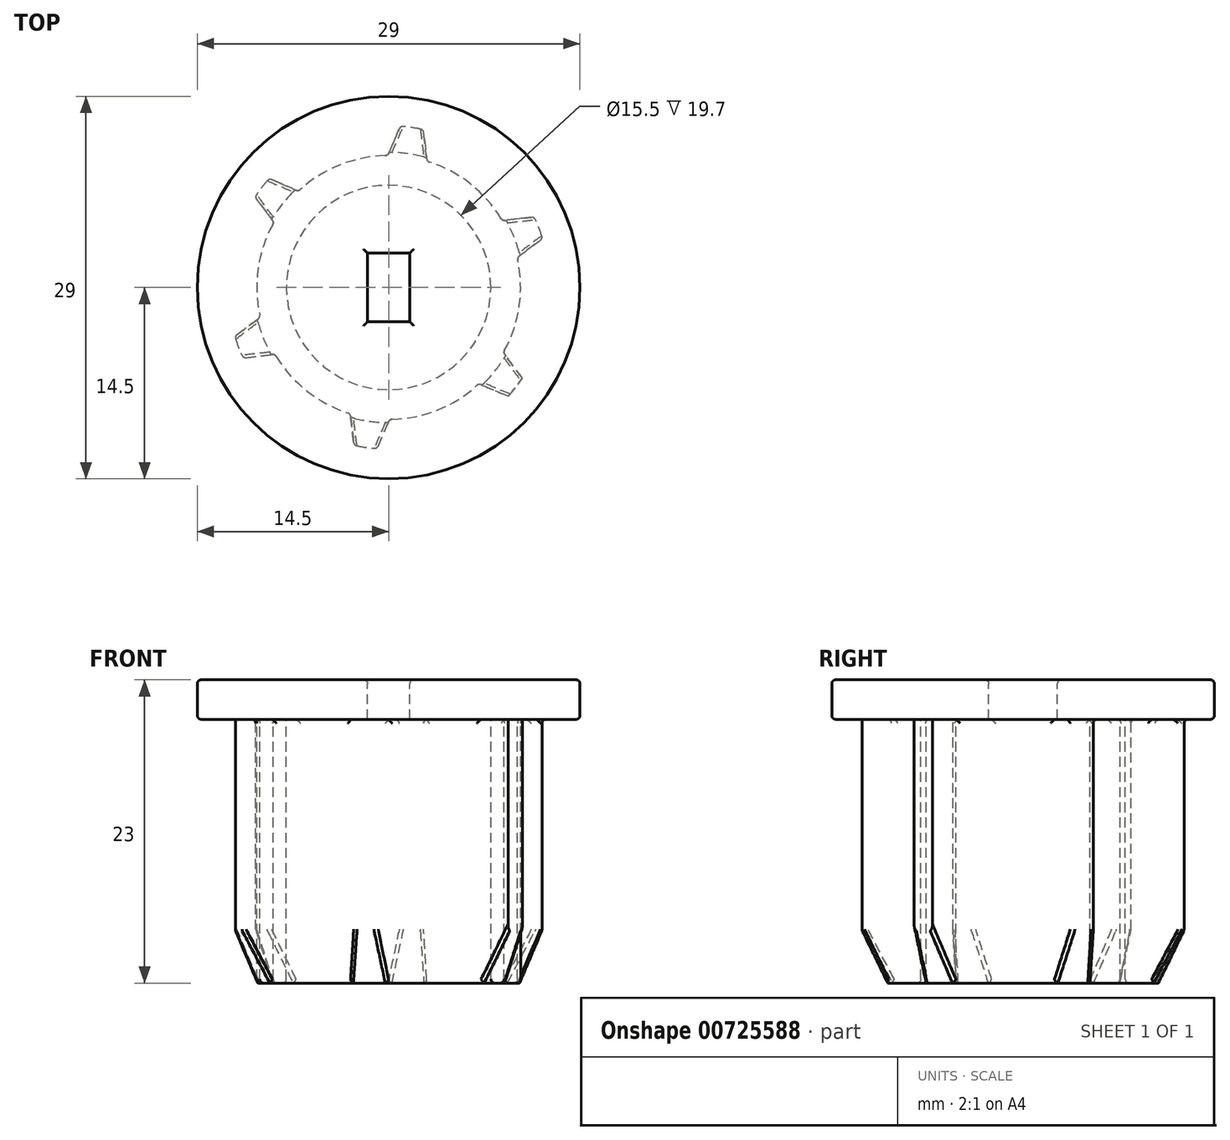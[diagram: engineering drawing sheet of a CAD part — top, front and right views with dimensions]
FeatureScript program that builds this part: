
annotation { "Feature Type Name" : "Feature", "Feature Type Description" : "" }
export const myFeature = defineFeature(function(context is Context, id is Id, definition is map)
    precondition{}
    {
        {
            var Q0;
            Q0=qCreatedBy(makeId("Top.planeOp"),FACE);
            var sketch = newSketch(context, id + "F0", { "sketchPlane" : qUnion([Q0])});
            skCircle(sketch, "E0", {"center": v(-16.6, 0) * mm, "radius": 14.5 * mm});
            skCircle(sketch, "E1", {"center": v(-16.6, 0) * mm, "radius": 12.25 * mm});
            skCircle(sketch, "E2", {"center": v(-16.6, 0) * mm, "radius": 4 * mm, "construction": true});
            skLineSegment(sketch, "E3.bottom", {"start": v(-18.2, -2.6) * mm, "end": v(-15, -2.6) * mm});
            skLineSegment(sketch, "E3.top", {"start": v(-18.2, 2.6) * mm, "end": v(-15, 2.6) * mm});
            skLineSegment(sketch, "E3.left", {"start": v(-18.2, -2.6) * mm, "end": v(-18.2, 2.6) * mm});
            skLineSegment(sketch, "E3.right", {"start": v(-15, -2.6) * mm, "end": v(-15, 2.6) * mm});
            skCircle(sketch, "E4.cCircle", {"center": v(-16.6, 0) * mm, "radius": 15 * mm, "construction": true});
            skLineSegment(sketch, "E4.0", {"start": v(-6.99, 12.2) * mm, "end": v(-2.18, 5.76) * mm});
            skLineSegment(sketch, "E4.1", {"start": v(-2.18, 5.76) * mm, "end": v(-1.23, -2.23) * mm});
            skLineSegment(sketch, "E4.2", {"start": v(-1.23, -2.23) * mm, "end": v(-4.4, -9.61) * mm});
            skLineSegment(sketch, "E4.3", {"start": v(-4.4, -9.61) * mm, "end": v(-10.84, -14.42) * mm});
            skLineSegment(sketch, "E4.4", {"start": v(-10.84, -14.42) * mm, "end": v(-18.83, -15.37) * mm});
            skLineSegment(sketch, "E4.5", {"start": v(-18.83, -15.37) * mm, "end": v(-26.21, -12.2) * mm});
            skLineSegment(sketch, "E4.6", {"start": v(-26.21, -12.2) * mm, "end": v(-31.02, -5.76) * mm});
            skLineSegment(sketch, "E4.7", {"start": v(-31.02, -5.76) * mm, "end": v(-31.97, 2.23) * mm});
            skLineSegment(sketch, "E4.8", {"start": v(-31.97, 2.23) * mm, "end": v(-28.8, 9.61) * mm});
            skLineSegment(sketch, "E4.9", {"start": v(-28.8, 9.61) * mm, "end": v(-22.36, 14.42) * mm});
            skLineSegment(sketch, "E4.10", {"start": v(-22.36, 14.42) * mm, "end": v(-14.37, 15.37) * mm});
            skLineSegment(sketch, "E4.11", {"start": v(-14.37, 15.37) * mm, "end": v(-6.99, 12.2) * mm});
            skPoint(sketch, "E4.0.midPoint", {"position": v(-4.58, 8.98) * mm});
            skLineSegment(sketch, "E5", {"start": v(-18.83, -15.37) * mm, "end": v(-20.57, -0.47) * mm});
            skLineSegment(sketch, "E6", {"start": v(-18.83, -15.37) * mm, "end": v(-12.92, -1.57) * mm});
            skLineSegment(sketch, "E7", {"start": v(-4.4, -9.61) * mm, "end": v(-18.18, -3.67) * mm});
            skLineSegment(sketch, "E8", {"start": v(-4.4, -9.61) * mm, "end": v(-13.4, 2.4) * mm});
            skLineSegment(sketch, "E9", {"start": v(-2.18, 5.76) * mm, "end": v(-14.21, -3.2) * mm});
            skLineSegment(sketch, "E10", {"start": v(-2.18, 5.76) * mm, "end": v(-17.08, 3.97) * mm});
            skLineSegment(sketch, "E11", {"start": v(-14.37, 15.37) * mm, "end": v(-12.63, 0.47) * mm});
            skLineSegment(sketch, "E12", {"start": v(-14.37, 15.37) * mm, "end": v(-20.28, 1.57) * mm});
            skLineSegment(sketch, "E13", {"start": v(-28.8, 9.61) * mm, "end": v(-15.02, 3.67) * mm});
            skLineSegment(sketch, "E14", {"start": v(-28.8, 9.61) * mm, "end": v(-19.8, -2.4) * mm});
            skLineSegment(sketch, "E15", {"start": v(-31.02, -5.76) * mm, "end": v(-18.99, 3.2) * mm});
            skLineSegment(sketch, "E16", {"start": v(-31.02, -5.76) * mm, "end": v(-16.12, -3.97) * mm});
            skCircle(sketch, "E17", {"center": v(-16.6, 0) * mm, "radius": 10 * mm});
            skCircle(sketch, "E18", {"center": v(-16.6, 0) * mm, "radius": 7.75 * mm});
            skSolve(sketch);
        }
        {
            var Q0;
            Q0=qCreatedBy(makeId("Front.planeOp"),FACE);
            var sketch = newSketch(context, id + "F1", { "sketchPlane" : qUnion([Q0])});
            skLineSegment(sketch, "E19", {"start": v(-32.68, -23) * mm, "end": v(-0.52, -23) * mm});
            skLineSegment(sketch, "E20", {"start": v(-32.68, -20) * mm, "end": v(-0.52, -20) * mm});
            skLineSegment(sketch, "E21", {"start": v(-32.68, -3) * mm, "end": v(-0.52, -3) * mm});
            skLineSegment(sketch, "E22", {"start": v(-32.68, 0) * mm, "end": v(-0.52, 0) * mm});
            skSolve(sketch);
        }
        {
            var Q0;
            {var subQ0=sQuery(id+"F0.wireOp",EDGE,"E17");var subQ1=sQuery(id+"F0.wireOp",EDGE,"E10");var subQ2=makeQuery(id+"F0.imprint","INTERSECT",VERTEX,{"derivedFrom":[subQ1,subQ0]});Q0=makeQuery(id+"F0.imprint","IMPRINT",FACE,{"disambiguationData":[TD([[makeQuery(id+"F0.imprint","IMPRINT",EDGE,{"disambiguationData":[TD([[subQ2,-1.0]])],"derivedFrom":subQ1}),-1.0]])]});}
            var Q1;
            {var subQ0=sQuery(id+"F0.wireOp",EDGE,"E10");var subQ1=sQuery(id+"F0.wireOp",EDGE,"E1");var subQ2=makeQuery(id+"F0.imprint","INTERSECT",VERTEX,{"derivedFrom":[subQ1,subQ0]});Q1=makeQuery(id+"F0.imprint","IMPRINT",FACE,{"disambiguationData":[TD([[makeQuery(id+"F0.imprint","IMPRINT",EDGE,{"disambiguationData":[TD([[subQ2,1.0]])],"derivedFrom":subQ1}),1.0]])]});}
            var Q2;
            {var subQ0=sQuery(id+"F0.wireOp",EDGE,"E17");var subQ1=sQuery(id+"F0.wireOp",EDGE,"E9");var subQ2=makeQuery(id+"F0.imprint","INTERSECT",VERTEX,{"derivedFrom":[subQ1,subQ0]});Q2=makeQuery(id+"F0.imprint","IMPRINT",FACE,{"disambiguationData":[TD([[makeQuery(id+"F0.imprint","IMPRINT",EDGE,{"disambiguationData":[TD([[subQ2,-1.0]])],"derivedFrom":subQ1}),-1.0]])]});}
            var Q3;
            {var subQ0=sQuery(id+"F0.wireOp",EDGE,"E17");var subQ1=sQuery(id+"F0.wireOp",EDGE,"E8");var subQ2=makeQuery(id+"F0.imprint","INTERSECT",VERTEX,{"derivedFrom":[subQ1,subQ0]});Q3=makeQuery(id+"F0.imprint","IMPRINT",FACE,{"disambiguationData":[TD([[makeQuery(id+"F0.imprint","IMPRINT",EDGE,{"disambiguationData":[TD([[subQ2,-1.0]])],"derivedFrom":subQ1}),-1.0]])]});}
            var Q4;
            {var subQ0=sQuery(id+"F0.wireOp",EDGE,"E7");var subQ1=sQuery(id+"F0.wireOp",EDGE,"E1");var subQ2=makeQuery(id+"F0.imprint","INTERSECT",VERTEX,{"derivedFrom":[subQ1,subQ0]});Q4=makeQuery(id+"F0.imprint","IMPRINT",FACE,{"disambiguationData":[TD([[makeQuery(id+"F0.imprint","IMPRINT",EDGE,{"disambiguationData":[TD([[subQ2,-1.0]])],"derivedFrom":subQ1}),1.0]])]});}
            var Q5;
            {var subQ0=sQuery(id+"F0.wireOp",EDGE,"E17");var subQ1=sQuery(id+"F0.wireOp",EDGE,"E7");var subQ2=makeQuery(id+"F0.imprint","INTERSECT",VERTEX,{"derivedFrom":[subQ1,subQ0]});Q5=makeQuery(id+"F0.imprint","IMPRINT",FACE,{"disambiguationData":[TD([[makeQuery(id+"F0.imprint","IMPRINT",EDGE,{"disambiguationData":[TD([[subQ2,-1.0]])],"derivedFrom":subQ1}),-1.0]])]});}
            var Q6;
            {var subQ0=sQuery(id+"F0.wireOp",EDGE,"E17");var subQ1=sQuery(id+"F0.wireOp",EDGE,"E6");var subQ2=makeQuery(id+"F0.imprint","INTERSECT",VERTEX,{"derivedFrom":[subQ1,subQ0]});Q6=makeQuery(id+"F0.imprint","IMPRINT",FACE,{"disambiguationData":[TD([[makeQuery(id+"F0.imprint","IMPRINT",EDGE,{"disambiguationData":[TD([[subQ2,-1.0]])],"derivedFrom":subQ1}),-1.0]])]});}
            var Q7;
            {var subQ0=sQuery(id+"F0.wireOp",EDGE,"E17");var subQ1=sQuery(id+"F0.wireOp",EDGE,"E5");var subQ2=makeQuery(id+"F0.imprint","INTERSECT",VERTEX,{"derivedFrom":[subQ1,subQ0]});Q7=makeQuery(id+"F0.imprint","IMPRINT",FACE,{"disambiguationData":[TD([[makeQuery(id+"F0.imprint","IMPRINT",EDGE,{"disambiguationData":[TD([[subQ2,-1.0]])],"derivedFrom":subQ1}),-1.0]])]});}
            var Q8;
            {var subQ0=sQuery(id+"F0.wireOp",EDGE,"E5");var subQ1=sQuery(id+"F0.wireOp",EDGE,"E1");var subQ2=makeQuery(id+"F0.imprint","INTERSECT",VERTEX,{"derivedFrom":[subQ1,subQ0]});Q8=makeQuery(id+"F0.imprint","IMPRINT",FACE,{"disambiguationData":[TD([[makeQuery(id+"F0.imprint","IMPRINT",EDGE,{"disambiguationData":[TD([[subQ2,-1.0]])],"derivedFrom":subQ1}),1.0]])]});}
            var Q9;
            {var subQ0=sQuery(id+"F0.wireOp",EDGE,"E17");var subQ1=sQuery(id+"F0.wireOp",EDGE,"E5");var subQ2=makeQuery(id+"F0.imprint","INTERSECT",VERTEX,{"derivedFrom":[subQ1,subQ0]});Q9=makeQuery(id+"F0.imprint","IMPRINT",FACE,{"disambiguationData":[TD([[makeQuery(id+"F0.imprint","IMPRINT",EDGE,{"disambiguationData":[TD([[subQ2,-1.0]])],"derivedFrom":subQ1}),1.0]])]});}
            var Q10;
            {var subQ0=sQuery(id+"F0.wireOp",EDGE,"E17");var subQ1=sQuery(id+"F0.wireOp",EDGE,"E15");var subQ2=makeQuery(id+"F0.imprint","INTERSECT",VERTEX,{"derivedFrom":[subQ1,subQ0]});Q10=makeQuery(id+"F0.imprint","IMPRINT",FACE,{"disambiguationData":[TD([[makeQuery(id+"F0.imprint","IMPRINT",EDGE,{"disambiguationData":[TD([[subQ2,-1.0]])],"derivedFrom":subQ1}),-1.0]])]});}
            var Q11;
            {var subQ0=sQuery(id+"F0.wireOp",EDGE,"E15");var subQ1=sQuery(id+"F0.wireOp",EDGE,"E1");var subQ2=makeQuery(id+"F0.imprint","INTERSECT",VERTEX,{"derivedFrom":[subQ1,subQ0]});Q11=makeQuery(id+"F0.imprint","IMPRINT",FACE,{"disambiguationData":[TD([[makeQuery(id+"F0.imprint","IMPRINT",EDGE,{"disambiguationData":[TD([[subQ2,-1.0]])],"derivedFrom":subQ1}),1.0]])]});}
            var Q12;
            {var subQ0=sQuery(id+"F0.wireOp",EDGE,"E17");var subQ1=sQuery(id+"F0.wireOp",EDGE,"E14");var subQ2=makeQuery(id+"F0.imprint","INTERSECT",VERTEX,{"derivedFrom":[subQ1,subQ0]});Q12=makeQuery(id+"F0.imprint","IMPRINT",FACE,{"disambiguationData":[TD([[makeQuery(id+"F0.imprint","IMPRINT",EDGE,{"disambiguationData":[TD([[subQ2,-1.0]])],"derivedFrom":subQ1}),-1.0]])]});}
            var Q13;
            {var subQ0=sQuery(id+"F0.wireOp",EDGE,"E17");var subQ1=sQuery(id+"F0.wireOp",EDGE,"E13");var subQ2=makeQuery(id+"F0.imprint","INTERSECT",VERTEX,{"derivedFrom":[subQ1,subQ0]});Q13=makeQuery(id+"F0.imprint","IMPRINT",FACE,{"disambiguationData":[TD([[makeQuery(id+"F0.imprint","IMPRINT",EDGE,{"disambiguationData":[TD([[subQ2,-1.0]])],"derivedFrom":subQ1}),-1.0]])]});}
            var Q14;
            {var subQ0=sQuery(id+"F0.wireOp",EDGE,"E13");var subQ1=sQuery(id+"F0.wireOp",EDGE,"E1");var subQ2=makeQuery(id+"F0.imprint","INTERSECT",VERTEX,{"derivedFrom":[subQ1,subQ0]});Q14=makeQuery(id+"F0.imprint","IMPRINT",FACE,{"disambiguationData":[TD([[makeQuery(id+"F0.imprint","IMPRINT",EDGE,{"disambiguationData":[TD([[subQ2,-1.0]])],"derivedFrom":subQ1}),1.0]])]});}
            var Q15;
            {var subQ0=sQuery(id+"F0.wireOp",EDGE,"E17");var subQ1=sQuery(id+"F0.wireOp",EDGE,"E12");var subQ2=makeQuery(id+"F0.imprint","INTERSECT",VERTEX,{"derivedFrom":[subQ1,subQ0]});Q15=makeQuery(id+"F0.imprint","IMPRINT",FACE,{"disambiguationData":[TD([[makeQuery(id+"F0.imprint","IMPRINT",EDGE,{"disambiguationData":[TD([[subQ2,-1.0]])],"derivedFrom":subQ1}),-1.0]])]});}
            var Q16;
            {var subQ0=sQuery(id+"F0.wireOp",EDGE,"E17");var subQ1=sQuery(id+"F0.wireOp",EDGE,"E11");var subQ2=makeQuery(id+"F0.imprint","INTERSECT",VERTEX,{"derivedFrom":[subQ1,subQ0]});Q16=makeQuery(id+"F0.imprint","IMPRINT",FACE,{"disambiguationData":[TD([[makeQuery(id+"F0.imprint","IMPRINT",EDGE,{"disambiguationData":[TD([[subQ2,-1.0]])],"derivedFrom":subQ1}),-1.0]])]});}
            var Q17;
            {var subQ0=sQuery(id+"F0.wireOp",EDGE,"E11");var subQ1=sQuery(id+"F0.wireOp",EDGE,"E1");var subQ2=makeQuery(id+"F0.imprint","INTERSECT",VERTEX,{"derivedFrom":[subQ1,subQ0]});Q17=makeQuery(id+"F0.imprint","IMPRINT",FACE,{"disambiguationData":[TD([[makeQuery(id+"F0.imprint","IMPRINT",EDGE,{"disambiguationData":[TD([[subQ2,-1.0]])],"derivedFrom":subQ1}),1.0]])]});}
            var Q18;
            Q18=sQuery(id+"F1.wireOp",VERTEX,"E19.start");
            extrude(context, id + "F2", {"entities" : qUnion([Q0, Q1, Q2, Q3, Q4, Q5, Q6, Q7, Q8, Q9, Q10, Q11, Q12, Q13, Q14, Q15, Q16, Q17]), "endBound" : BoundingType.UP_TO_VERTEX, "oppositeDirection" : true, "depth" : 25 * mm, "endBoundEntityVertex" : qUnion([Q18]), "offsetDistance" : 25 * mm});
        }
        {
            var Q0;
            {var subQ0=sQuery(id+"F0.wireOp",EDGE,"E12");var subQ1=sQuery(id+"F0.wireOp",EDGE,"E1");var subQ2=makeQuery(id+"F0.imprint","INTERSECT",VERTEX,{"derivedFrom":[subQ1,subQ0]});Q0=makeQuery(id+"F0.imprint","IMPRINT",FACE,{"disambiguationData":[TD([[makeQuery(id+"F0.imprint","IMPRINT",EDGE,{"disambiguationData":[TD([[subQ2,-1.0]])],"derivedFrom":subQ1}),1.0]])]});}
            var Q1;
            {var subQ0=sQuery(id+"F0.wireOp",EDGE,"E12");var subQ1=sQuery(id+"F0.wireOp",EDGE,"E0");var subQ2=makeQuery(id+"F0.imprint","INTERSECT",VERTEX,{"derivedFrom":[subQ1,subQ0]});Q1=makeQuery(id+"F0.imprint","IMPRINT",FACE,{"disambiguationData":[TD([[makeQuery(id+"F0.imprint","IMPRINT",EDGE,{"disambiguationData":[TD([[subQ2,-1.0]])],"derivedFrom":subQ1}),1.0]])]});}
            var Q2;
            {var subQ0=sQuery(id+"F0.wireOp",EDGE,"E11");var subQ1=sQuery(id+"F0.wireOp",EDGE,"E0");var subQ2=makeQuery(id+"F0.imprint","INTERSECT",VERTEX,{"derivedFrom":[subQ1,subQ0]});Q2=makeQuery(id+"F0.imprint","IMPRINT",FACE,{"disambiguationData":[TD([[makeQuery(id+"F0.imprint","IMPRINT",EDGE,{"disambiguationData":[TD([[subQ2,-1.0]])],"derivedFrom":subQ1}),1.0]])]});}
            var Q3;
            {var subQ0=sQuery(id+"F0.wireOp",EDGE,"E10");var subQ1=sQuery(id+"F0.wireOp",EDGE,"E0");var subQ2=makeQuery(id+"F0.imprint","INTERSECT",VERTEX,{"derivedFrom":[subQ1,subQ0]});Q3=makeQuery(id+"F0.imprint","IMPRINT",FACE,{"disambiguationData":[TD([[makeQuery(id+"F0.imprint","IMPRINT",EDGE,{"disambiguationData":[TD([[subQ2,-1.0]])],"derivedFrom":subQ1}),1.0]])]});}
            var Q4;
            {var subQ0=sQuery(id+"F0.wireOp",EDGE,"E10");var subQ1=sQuery(id+"F0.wireOp",EDGE,"E1");var subQ2=makeQuery(id+"F0.imprint","INTERSECT",VERTEX,{"derivedFrom":[subQ1,subQ0]});Q4=makeQuery(id+"F0.imprint","IMPRINT",FACE,{"disambiguationData":[TD([[makeQuery(id+"F0.imprint","IMPRINT",EDGE,{"disambiguationData":[TD([[subQ2,-1.0]])],"derivedFrom":subQ1}),1.0]])]});}
            var Q5;
            {var subQ0=sQuery(id+"F0.wireOp",EDGE,"E11");var subQ1=sQuery(id+"F0.wireOp",EDGE,"E1");var subQ2=makeQuery(id+"F0.imprint","INTERSECT",VERTEX,{"derivedFrom":[subQ1,subQ0]});Q5=makeQuery(id+"F0.imprint","IMPRINT",FACE,{"disambiguationData":[TD([[makeQuery(id+"F0.imprint","IMPRINT",EDGE,{"disambiguationData":[TD([[subQ2,-1.0]])],"derivedFrom":subQ1}),1.0]])]});}
            var Q6;
            {var subQ0=sQuery(id+"F0.wireOp",EDGE,"E17");var subQ1=sQuery(id+"F0.wireOp",EDGE,"E10");var subQ2=makeQuery(id+"F0.imprint","INTERSECT",VERTEX,{"derivedFrom":[subQ1,subQ0]});Q6=makeQuery(id+"F0.imprint","IMPRINT",FACE,{"disambiguationData":[TD([[makeQuery(id+"F0.imprint","IMPRINT",EDGE,{"disambiguationData":[TD([[subQ2,-1.0]])],"derivedFrom":subQ1}),-1.0]])]});}
            var Q7;
            {var subQ0=sQuery(id+"F0.wireOp",EDGE,"E17");var subQ1=sQuery(id+"F0.wireOp",EDGE,"E9");var subQ2=makeQuery(id+"F0.imprint","INTERSECT",VERTEX,{"derivedFrom":[subQ1,subQ0]});Q7=makeQuery(id+"F0.imprint","IMPRINT",FACE,{"disambiguationData":[TD([[makeQuery(id+"F0.imprint","IMPRINT",EDGE,{"disambiguationData":[TD([[subQ2,-1.0]])],"derivedFrom":subQ1}),-1.0]])]});}
            var Q8;
            {var subQ0=sQuery(id+"F0.wireOp",EDGE,"E10");var subQ1=sQuery(id+"F0.wireOp",EDGE,"E1");var subQ2=makeQuery(id+"F0.imprint","INTERSECT",VERTEX,{"derivedFrom":[subQ1,subQ0]});Q8=makeQuery(id+"F0.imprint","IMPRINT",FACE,{"disambiguationData":[TD([[makeQuery(id+"F0.imprint","IMPRINT",EDGE,{"disambiguationData":[TD([[subQ2,1.0]])],"derivedFrom":subQ1}),1.0]])]});}
            var Q9;
            {var subQ0=sQuery(id+"F0.wireOp",EDGE,"E10");var subQ1=sQuery(id+"F0.wireOp",EDGE,"E0");var subQ2=makeQuery(id+"F0.imprint","INTERSECT",VERTEX,{"derivedFrom":[subQ1,subQ0]});Q9=makeQuery(id+"F0.imprint","IMPRINT",FACE,{"disambiguationData":[TD([[makeQuery(id+"F0.imprint","IMPRINT",EDGE,{"disambiguationData":[TD([[subQ2,1.0]])],"derivedFrom":subQ1}),1.0]])]});}
            var Q10;
            {var subQ0=sQuery(id+"F0.wireOp",EDGE,"E9");var subQ1=sQuery(id+"F0.wireOp",EDGE,"E1");var subQ2=makeQuery(id+"F0.imprint","INTERSECT",VERTEX,{"derivedFrom":[subQ1,subQ0]});Q10=makeQuery(id+"F0.imprint","IMPRINT",FACE,{"disambiguationData":[TD([[makeQuery(id+"F0.imprint","IMPRINT",EDGE,{"disambiguationData":[TD([[subQ2,1.0]])],"derivedFrom":subQ1}),1.0]])]});}
            var Q11;
            {var subQ0=sQuery(id+"F0.wireOp",EDGE,"E6");var subQ1=sQuery(id+"F0.wireOp",EDGE,"E0");var subQ2=makeQuery(id+"F0.imprint","INTERSECT",VERTEX,{"derivedFrom":[subQ1,subQ0]});Q11=makeQuery(id+"F0.imprint","IMPRINT",FACE,{"disambiguationData":[TD([[makeQuery(id+"F0.imprint","IMPRINT",EDGE,{"disambiguationData":[TD([[subQ2,-1.0]])],"derivedFrom":subQ1}),1.0]])]});}
            var Q12;
            {var subQ0=sQuery(id+"F0.wireOp",EDGE,"E5");var subQ1=sQuery(id+"F0.wireOp",EDGE,"E0");var subQ2=makeQuery(id+"F0.imprint","INTERSECT",VERTEX,{"derivedFrom":[subQ1,subQ0]});Q12=makeQuery(id+"F0.imprint","IMPRINT",FACE,{"disambiguationData":[TD([[makeQuery(id+"F0.imprint","IMPRINT",EDGE,{"disambiguationData":[TD([[subQ2,-1.0]])],"derivedFrom":subQ1}),1.0]])]});}
            var Q13;
            {var subQ0=sQuery(id+"F0.wireOp",EDGE,"E5");var subQ1=sQuery(id+"F0.wireOp",EDGE,"E1");var subQ2=makeQuery(id+"F0.imprint","INTERSECT",VERTEX,{"derivedFrom":[subQ1,subQ0]});Q13=makeQuery(id+"F0.imprint","IMPRINT",FACE,{"disambiguationData":[TD([[makeQuery(id+"F0.imprint","IMPRINT",EDGE,{"disambiguationData":[TD([[subQ2,-1.0]])],"derivedFrom":subQ1}),1.0]])]});}
            var Q14;
            {var subQ0=sQuery(id+"F0.wireOp",EDGE,"E15");var subQ1=sQuery(id+"F0.wireOp",EDGE,"E1");var subQ2=makeQuery(id+"F0.imprint","INTERSECT",VERTEX,{"derivedFrom":[subQ1,subQ0]});Q14=makeQuery(id+"F0.imprint","IMPRINT",FACE,{"disambiguationData":[TD([[makeQuery(id+"F0.imprint","IMPRINT",EDGE,{"disambiguationData":[TD([[subQ2,-1.0]])],"derivedFrom":subQ1}),1.0]])]});}
            var Q15;
            {var subQ0=sQuery(id+"F0.wireOp",EDGE,"E17");var subQ1=sQuery(id+"F0.wireOp",EDGE,"E15");var subQ2=makeQuery(id+"F0.imprint","INTERSECT",VERTEX,{"derivedFrom":[subQ1,subQ0]});Q15=makeQuery(id+"F0.imprint","IMPRINT",FACE,{"disambiguationData":[TD([[makeQuery(id+"F0.imprint","IMPRINT",EDGE,{"disambiguationData":[TD([[subQ2,-1.0]])],"derivedFrom":subQ1}),-1.0]])]});}
            var Q16;
            {var subQ0=sQuery(id+"F0.wireOp",EDGE,"E9");var subQ1=sQuery(id+"F0.wireOp",EDGE,"E0");var subQ2=makeQuery(id+"F0.imprint","INTERSECT",VERTEX,{"derivedFrom":[subQ1,subQ0]});Q16=makeQuery(id+"F0.imprint","IMPRINT",FACE,{"disambiguationData":[TD([[makeQuery(id+"F0.imprint","IMPRINT",EDGE,{"disambiguationData":[TD([[subQ2,1.0]])],"derivedFrom":subQ1}),1.0]])]});}
            var Q17;
            {var subQ0=sQuery(id+"F0.wireOp",EDGE,"E7");var subQ1=sQuery(id+"F0.wireOp",EDGE,"E0");var subQ2=makeQuery(id+"F0.imprint","INTERSECT",VERTEX,{"derivedFrom":[subQ1,subQ0]});Q17=makeQuery(id+"F0.imprint","IMPRINT",FACE,{"disambiguationData":[TD([[makeQuery(id+"F0.imprint","IMPRINT",EDGE,{"disambiguationData":[TD([[subQ2,-1.0]])],"derivedFrom":subQ1}),1.0]])]});}
            var Q18;
            {var subQ0=sQuery(id+"F0.wireOp",EDGE,"E7");var subQ1=sQuery(id+"F0.wireOp",EDGE,"E1");var subQ2=makeQuery(id+"F0.imprint","INTERSECT",VERTEX,{"derivedFrom":[subQ1,subQ0]});Q18=makeQuery(id+"F0.imprint","IMPRINT",FACE,{"disambiguationData":[TD([[makeQuery(id+"F0.imprint","IMPRINT",EDGE,{"disambiguationData":[TD([[subQ2,-1.0]])],"derivedFrom":subQ1}),1.0]])]});}
            var Q19;
            {var subQ0=sQuery(id+"F0.wireOp",EDGE,"E6");var subQ1=sQuery(id+"F0.wireOp",EDGE,"E1");var subQ2=makeQuery(id+"F0.imprint","INTERSECT",VERTEX,{"derivedFrom":[subQ1,subQ0]});Q19=makeQuery(id+"F0.imprint","IMPRINT",FACE,{"disambiguationData":[TD([[makeQuery(id+"F0.imprint","IMPRINT",EDGE,{"disambiguationData":[TD([[subQ2,-1.0]])],"derivedFrom":subQ1}),1.0]])]});}
            var Q20;
            {var subQ0=sQuery(id+"F0.wireOp",EDGE,"E16");var subQ1=sQuery(id+"F0.wireOp",EDGE,"E1");var subQ2=makeQuery(id+"F0.imprint","INTERSECT",VERTEX,{"derivedFrom":[subQ1,subQ0]});Q20=makeQuery(id+"F0.imprint","IMPRINT",FACE,{"disambiguationData":[TD([[makeQuery(id+"F0.imprint","IMPRINT",EDGE,{"disambiguationData":[TD([[subQ2,-1.0]])],"derivedFrom":subQ1}),1.0]])]});}
            var Q21;
            {var subQ0=sQuery(id+"F0.wireOp",EDGE,"E16");var subQ1=sQuery(id+"F0.wireOp",EDGE,"E0");var subQ2=makeQuery(id+"F0.imprint","INTERSECT",VERTEX,{"derivedFrom":[subQ1,subQ0]});Q21=makeQuery(id+"F0.imprint","IMPRINT",FACE,{"disambiguationData":[TD([[makeQuery(id+"F0.imprint","IMPRINT",EDGE,{"disambiguationData":[TD([[subQ2,-1.0]])],"derivedFrom":subQ1}),1.0]])]});}
            var Q22;
            {var subQ0=sQuery(id+"F0.wireOp",EDGE,"E15");var subQ1=sQuery(id+"F0.wireOp",EDGE,"E0");var subQ2=makeQuery(id+"F0.imprint","INTERSECT",VERTEX,{"derivedFrom":[subQ1,subQ0]});Q22=makeQuery(id+"F0.imprint","IMPRINT",FACE,{"disambiguationData":[TD([[makeQuery(id+"F0.imprint","IMPRINT",EDGE,{"disambiguationData":[TD([[subQ2,-1.0]])],"derivedFrom":subQ1}),1.0]])]});}
            var Q23;
            {var subQ0=sQuery(id+"F0.wireOp",EDGE,"E14");var subQ1=sQuery(id+"F0.wireOp",EDGE,"E0");var subQ2=makeQuery(id+"F0.imprint","INTERSECT",VERTEX,{"derivedFrom":[subQ1,subQ0]});Q23=makeQuery(id+"F0.imprint","IMPRINT",FACE,{"disambiguationData":[TD([[makeQuery(id+"F0.imprint","IMPRINT",EDGE,{"disambiguationData":[TD([[subQ2,-1.0]])],"derivedFrom":subQ1}),1.0]])]});}
            var Q24;
            {var subQ0=sQuery(id+"F0.wireOp",EDGE,"E14");var subQ1=sQuery(id+"F0.wireOp",EDGE,"E1");var subQ2=makeQuery(id+"F0.imprint","INTERSECT",VERTEX,{"derivedFrom":[subQ1,subQ0]});Q24=makeQuery(id+"F0.imprint","IMPRINT",FACE,{"disambiguationData":[TD([[makeQuery(id+"F0.imprint","IMPRINT",EDGE,{"disambiguationData":[TD([[subQ2,-1.0]])],"derivedFrom":subQ1}),1.0]])]});}
            var Q25;
            {var subQ0=sQuery(id+"F0.wireOp",EDGE,"E17");var subQ1=sQuery(id+"F0.wireOp",EDGE,"E14");var subQ2=makeQuery(id+"F0.imprint","INTERSECT",VERTEX,{"derivedFrom":[subQ1,subQ0]});Q25=makeQuery(id+"F0.imprint","IMPRINT",FACE,{"disambiguationData":[TD([[makeQuery(id+"F0.imprint","IMPRINT",EDGE,{"disambiguationData":[TD([[subQ2,-1.0]])],"derivedFrom":subQ1}),-1.0]])]});}
            var Q26;
            {var subQ0=sQuery(id+"F0.wireOp",EDGE,"E13");var subQ1=sQuery(id+"F0.wireOp",EDGE,"E0");var subQ2=makeQuery(id+"F0.imprint","INTERSECT",VERTEX,{"derivedFrom":[subQ1,subQ0]});Q26=makeQuery(id+"F0.imprint","IMPRINT",FACE,{"disambiguationData":[TD([[makeQuery(id+"F0.imprint","IMPRINT",EDGE,{"disambiguationData":[TD([[subQ2,-1.0]])],"derivedFrom":subQ1}),1.0]])]});}
            var Q27;
            {var subQ0=sQuery(id+"F0.wireOp",EDGE,"E13");var subQ1=sQuery(id+"F0.wireOp",EDGE,"E1");var subQ2=makeQuery(id+"F0.imprint","INTERSECT",VERTEX,{"derivedFrom":[subQ1,subQ0]});Q27=makeQuery(id+"F0.imprint","IMPRINT",FACE,{"disambiguationData":[TD([[makeQuery(id+"F0.imprint","IMPRINT",EDGE,{"disambiguationData":[TD([[subQ2,-1.0]])],"derivedFrom":subQ1}),1.0]])]});}
            var Q28;
            {var subQ0=sQuery(id+"F0.wireOp",EDGE,"E17");var subQ1=sQuery(id+"F0.wireOp",EDGE,"E13");var subQ2=makeQuery(id+"F0.imprint","INTERSECT",VERTEX,{"derivedFrom":[subQ1,subQ0]});Q28=makeQuery(id+"F0.imprint","IMPRINT",FACE,{"disambiguationData":[TD([[makeQuery(id+"F0.imprint","IMPRINT",EDGE,{"disambiguationData":[TD([[subQ2,-1.0]])],"derivedFrom":subQ1}),-1.0]])]});}
            var Q29;
            {var subQ0=sQuery(id+"F0.wireOp",EDGE,"E17");var subQ1=sQuery(id+"F0.wireOp",EDGE,"E12");var subQ2=makeQuery(id+"F0.imprint","INTERSECT",VERTEX,{"derivedFrom":[subQ1,subQ0]});Q29=makeQuery(id+"F0.imprint","IMPRINT",FACE,{"disambiguationData":[TD([[makeQuery(id+"F0.imprint","IMPRINT",EDGE,{"disambiguationData":[TD([[subQ2,-1.0]])],"derivedFrom":subQ1}),-1.0]])]});}
            var Q30;
            {var subQ0=sQuery(id+"F0.wireOp",EDGE,"E17");var subQ1=sQuery(id+"F0.wireOp",EDGE,"E11");var subQ2=makeQuery(id+"F0.imprint","INTERSECT",VERTEX,{"derivedFrom":[subQ1,subQ0]});Q30=makeQuery(id+"F0.imprint","IMPRINT",FACE,{"disambiguationData":[TD([[makeQuery(id+"F0.imprint","IMPRINT",EDGE,{"disambiguationData":[TD([[subQ2,-1.0]])],"derivedFrom":subQ1}),-1.0]])]});}
            var Q31;
            {var subQ0=sQuery(id+"F0.wireOp",EDGE,"E13");var subQ1=sQuery(id+"F0.wireOp",EDGE,"E10");var subQ2=makeQuery(id+"F0.imprint","INTERSECT",VERTEX,{"derivedFrom":[subQ1,subQ0]});Q31=makeQuery(id+"F0.imprint","IMPRINT",FACE,{"disambiguationData":[TD([[makeQuery(id+"F0.imprint","IMPRINT",EDGE,{"disambiguationData":[TD([[subQ2,1.0]])],"derivedFrom":subQ1}),-1.0]])]});}
            var Q32;
            {var subQ0=sQuery(id+"F0.wireOp",EDGE,"E18");var subQ1=sQuery(id+"F0.wireOp",EDGE,"E10");var subQ2=makeQuery(id+"F0.imprint","INTERSECT",VERTEX,{"derivedFrom":[subQ1,subQ0]});Q32=makeQuery(id+"F0.imprint","IMPRINT",FACE,{"disambiguationData":[TD([[makeQuery(id+"F0.imprint","IMPRINT",EDGE,{"disambiguationData":[TD([[subQ2,-1.0]])],"derivedFrom":subQ1}),-1.0]])]});}
            var Q33;
            {var subQ0=sQuery(id+"F0.wireOp",EDGE,"E11");var subQ1=sQuery(id+"F0.wireOp",EDGE,"E8");var subQ2=makeQuery(id+"F0.imprint","INTERSECT",VERTEX,{"derivedFrom":[subQ1,subQ0]});Q33=makeQuery(id+"F0.imprint","IMPRINT",FACE,{"disambiguationData":[TD([[makeQuery(id+"F0.imprint","IMPRINT",EDGE,{"disambiguationData":[TD([[subQ2,1.0]])],"derivedFrom":subQ1}),-1.0]])]});}
            var Q34;
            {var subQ0=sQuery(id+"F0.wireOp",EDGE,"E9");var subQ1=sQuery(id+"F0.wireOp",EDGE,"E6");var subQ2=makeQuery(id+"F0.imprint","INTERSECT",VERTEX,{"derivedFrom":[subQ1,subQ0]});Q34=makeQuery(id+"F0.imprint","IMPRINT",FACE,{"disambiguationData":[TD([[makeQuery(id+"F0.imprint","IMPRINT",EDGE,{"disambiguationData":[TD([[subQ2,1.0]])],"derivedFrom":subQ1}),-1.0]])]});}
            var Q35;
            {var subQ0=sQuery(id+"F0.wireOp",EDGE,"E17");var subQ1=sQuery(id+"F0.wireOp",EDGE,"E7");var subQ2=makeQuery(id+"F0.imprint","INTERSECT",VERTEX,{"derivedFrom":[subQ1,subQ0]});Q35=makeQuery(id+"F0.imprint","IMPRINT",FACE,{"disambiguationData":[TD([[makeQuery(id+"F0.imprint","IMPRINT",EDGE,{"disambiguationData":[TD([[subQ2,-1.0]])],"derivedFrom":subQ1}),-1.0]])]});}
            var Q36;
            {var subQ0=sQuery(id+"F0.wireOp",EDGE,"E17");var subQ1=sQuery(id+"F0.wireOp",EDGE,"E8");var subQ2=makeQuery(id+"F0.imprint","INTERSECT",VERTEX,{"derivedFrom":[subQ1,subQ0]});Q36=makeQuery(id+"F0.imprint","IMPRINT",FACE,{"disambiguationData":[TD([[makeQuery(id+"F0.imprint","IMPRINT",EDGE,{"disambiguationData":[TD([[subQ2,-1.0]])],"derivedFrom":subQ1}),-1.0]])]});}
            var Q37;
            {var subQ0=sQuery(id+"F0.wireOp",EDGE,"E17");var subQ1=sQuery(id+"F0.wireOp",EDGE,"E6");var subQ2=makeQuery(id+"F0.imprint","INTERSECT",VERTEX,{"derivedFrom":[subQ1,subQ0]});Q37=makeQuery(id+"F0.imprint","IMPRINT",FACE,{"disambiguationData":[TD([[makeQuery(id+"F0.imprint","IMPRINT",EDGE,{"disambiguationData":[TD([[subQ2,-1.0]])],"derivedFrom":subQ1}),-1.0]])]});}
            var Q38;
            {var subQ0=sQuery(id+"F0.wireOp",EDGE,"E18");var subQ1=sQuery(id+"F0.wireOp",EDGE,"E8");var subQ2=makeQuery(id+"F0.imprint","INTERSECT",VERTEX,{"derivedFrom":[subQ1,subQ0]});Q38=makeQuery(id+"F0.imprint","IMPRINT",FACE,{"disambiguationData":[TD([[makeQuery(id+"F0.imprint","IMPRINT",EDGE,{"disambiguationData":[TD([[subQ2,-1.0]])],"derivedFrom":subQ1}),-1.0]])]});}
            var Q39;
            Q39=makeQuery(id+"F0.imprint","IMPRINT",FACE,{"disambiguationData":[TD([[makeQuery(id+"F0.imprint","IMPRINT",EDGE,{"derivedFrom":sQuery(id+"F0.wireOp",EDGE,"E3.bottom")}),-1.0]])]});
            var Q40;
            {var subQ0=sQuery(id+"F0.wireOp",EDGE,"E17");var subQ1=sQuery(id+"F0.wireOp",EDGE,"E5");var subQ2=makeQuery(id+"F0.imprint","INTERSECT",VERTEX,{"derivedFrom":[subQ1,subQ0]});Q40=makeQuery(id+"F0.imprint","IMPRINT",FACE,{"disambiguationData":[TD([[makeQuery(id+"F0.imprint","IMPRINT",EDGE,{"disambiguationData":[TD([[subQ2,-1.0]])],"derivedFrom":subQ1}),-1.0]])]});}
            var Q41;
            {var subQ0=sQuery(id+"F0.wireOp",EDGE,"E17");var subQ1=sQuery(id+"F0.wireOp",EDGE,"E5");var subQ2=makeQuery(id+"F0.imprint","INTERSECT",VERTEX,{"derivedFrom":[subQ1,subQ0]});Q41=makeQuery(id+"F0.imprint","IMPRINT",FACE,{"disambiguationData":[TD([[makeQuery(id+"F0.imprint","IMPRINT",EDGE,{"disambiguationData":[TD([[subQ2,-1.0]])],"derivedFrom":subQ1}),1.0]])]});}
            var Q42;
            {var subQ3=sQuery(id+"F0.wireOp",EDGE,"E5");var subQ7=sQuery(id+"F0.wireOp",EDGE,"E18");var subQ9=makeQuery(id+"F0.imprint","INTERSECT",VERTEX,{"derivedFrom":[subQ3,subQ7]});Q42=makeQuery(id+"F0.imprint","IMPRINT",FACE,{"disambiguationData":[TD([[makeQuery(id+"F0.imprint","IMPRINT",EDGE,{"disambiguationData":[TD([[subQ9,-1.0]])],"derivedFrom":subQ3}),-1.0]])]});}
            var Q43;
            {var subQ1=sQuery(id+"F0.wireOp",EDGE,"E14");var subQ5=sQuery(id+"F0.wireOp",EDGE,"E5");var subQ6=makeQuery(id+"F0.imprint","INTERSECT",VERTEX,{"derivedFrom":[subQ5,subQ1]});Q43=makeQuery(id+"F0.imprint","IMPRINT",FACE,{"disambiguationData":[TD([[makeQuery(id+"F0.imprint","IMPRINT",EDGE,{"disambiguationData":[TD([[subQ6,1.0]])],"derivedFrom":subQ5}),1.0]])]});}
            var Q44;
            {var subQ0=sQuery(id+"F0.wireOp",EDGE,"E18");var subQ1=sQuery(id+"F0.wireOp",EDGE,"E6");var subQ2=makeQuery(id+"F0.imprint","INTERSECT",VERTEX,{"derivedFrom":[subQ1,subQ0]});Q44=makeQuery(id+"F0.imprint","IMPRINT",FACE,{"disambiguationData":[TD([[makeQuery(id+"F0.imprint","IMPRINT",EDGE,{"disambiguationData":[TD([[subQ2,-1.0]])],"derivedFrom":subQ1}),-1.0]])]});}
            var Q45;
            {var subQ0=sQuery(id+"F0.wireOp",EDGE,"E18");var subQ1=sQuery(id+"F0.wireOp",EDGE,"E5");var subQ2=makeQuery(id+"F0.imprint","INTERSECT",VERTEX,{"derivedFrom":[subQ1,subQ0]});Q45=makeQuery(id+"F0.imprint","IMPRINT",FACE,{"disambiguationData":[TD([[makeQuery(id+"F0.imprint","IMPRINT",EDGE,{"disambiguationData":[TD([[subQ2,-1.0]])],"derivedFrom":subQ1}),1.0]])]});}
            var Q46;
            {var subQ0=sQuery(id+"F0.wireOp",EDGE,"E15");var subQ1=sQuery(id+"F0.wireOp",EDGE,"E12");var subQ2=makeQuery(id+"F0.imprint","INTERSECT",VERTEX,{"derivedFrom":[subQ1,subQ0]});Q46=makeQuery(id+"F0.imprint","IMPRINT",FACE,{"disambiguationData":[TD([[makeQuery(id+"F0.imprint","IMPRINT",EDGE,{"disambiguationData":[TD([[subQ2,1.0]])],"derivedFrom":subQ1}),-1.0]])]});}
            var Q47;
            {var subQ0=sQuery(id+"F0.wireOp",EDGE,"E18");var subQ1=sQuery(id+"F0.wireOp",EDGE,"E12");var subQ2=makeQuery(id+"F0.imprint","INTERSECT",VERTEX,{"derivedFrom":[subQ1,subQ0]});Q47=makeQuery(id+"F0.imprint","IMPRINT",FACE,{"disambiguationData":[TD([[makeQuery(id+"F0.imprint","IMPRINT",EDGE,{"disambiguationData":[TD([[subQ2,-1.0]])],"derivedFrom":subQ1}),-1.0]])]});}
            var Q48;
            {var subQ0=sQuery(id+"F0.wireOp",EDGE,"E18");var subQ1=sQuery(id+"F0.wireOp",EDGE,"E14");var subQ2=makeQuery(id+"F0.imprint","INTERSECT",VERTEX,{"derivedFrom":[subQ1,subQ0]});Q48=makeQuery(id+"F0.imprint","IMPRINT",FACE,{"disambiguationData":[TD([[makeQuery(id+"F0.imprint","IMPRINT",EDGE,{"disambiguationData":[TD([[subQ2,-1.0]])],"derivedFrom":subQ1}),-1.0]])]});}
            var Q49;
            Q49=sQuery(id+"F1.wireOp",VERTEX,"E21.start");
            extrude(context, id + "F3", {"entities" : qUnion([Q0, Q1, Q2, Q3, Q4, Q5, Q6, Q7, Q8, Q9, Q10, Q11, Q12, Q13, Q14, Q15, Q16, Q17, Q18, Q19, Q20, Q21, Q22, Q23, Q24, Q25, Q26, Q27, Q28, Q29, Q30, Q31, Q32, Q33, Q34, Q35, Q36, Q37, Q38, Q39, Q40, Q41, Q42, Q43, Q44, Q45, Q46, Q47, Q48]), "operationType" : NewBodyOperationType.ADD, "endBound" : BoundingType.UP_TO_VERTEX, "oppositeDirection" : true, "depth" : 25 * mm, "endBoundEntityVertex" : qUnion([Q49]), "offsetDistance" : 25 * mm});
        }
        {
            var Q0;
            {var subQ0=sQuery(id+"F0.wireOp",EDGE,"E1");Q0=makeQuery(id+"F2.opExtrude","CAP_EDGE",EDGE,{"disambiguationData":[OSD([subQ0]),TDD([makeQuery(id+"F0.imprint","IMPRINT",EDGE,{"disambiguationData":[TD([[makeQuery(id+"F0.imprint","INTERSECT",VERTEX,{"derivedFrom":[subQ0,sQuery(id+"F0.wireOp",EDGE,"E5")]}),-1.0]])],"derivedFrom":subQ0})])],"isStart":false});}
            var Q1;
            {var subQ0=sQuery(id+"F0.wireOp",EDGE,"E1");Q1=makeQuery(id+"F2.opExtrude","CAP_EDGE",EDGE,{"disambiguationData":[OSD([subQ0]),TDD([makeQuery(id+"F0.imprint","IMPRINT",EDGE,{"disambiguationData":[TD([[makeQuery(id+"F0.imprint","INTERSECT",VERTEX,{"derivedFrom":[subQ0,sQuery(id+"F0.wireOp",EDGE,"E10")]}),1.0]])],"derivedFrom":subQ0})])],"isStart":false});}
            var Q2;
            {var subQ0=sQuery(id+"F0.wireOp",EDGE,"E1");Q2=makeQuery(id+"F2.opExtrude","CAP_EDGE",EDGE,{"disambiguationData":[OSD([subQ0]),TDD([makeQuery(id+"F0.imprint","IMPRINT",EDGE,{"disambiguationData":[TD([[makeQuery(id+"F0.imprint","INTERSECT",VERTEX,{"derivedFrom":[subQ0,sQuery(id+"F0.wireOp",EDGE,"E11")]}),-1.0]])],"derivedFrom":subQ0})])],"isStart":false});}
            var Q3;
            {var subQ0=sQuery(id+"F0.wireOp",EDGE,"E1");Q3=makeQuery(id+"F2.opExtrude","CAP_EDGE",EDGE,{"disambiguationData":[OSD([subQ0]),TDD([makeQuery(id+"F0.imprint","IMPRINT",EDGE,{"disambiguationData":[TD([[makeQuery(id+"F0.imprint","INTERSECT",VERTEX,{"derivedFrom":[subQ0,sQuery(id+"F0.wireOp",EDGE,"E13")]}),-1.0]])],"derivedFrom":subQ0})])],"isStart":false});}
            var Q4;
            {var subQ0=sQuery(id+"F0.wireOp",EDGE,"E1");Q4=makeQuery(id+"F2.opExtrude","CAP_EDGE",EDGE,{"disambiguationData":[OSD([subQ0]),TDD([makeQuery(id+"F0.imprint","IMPRINT",EDGE,{"disambiguationData":[TD([[makeQuery(id+"F0.imprint","INTERSECT",VERTEX,{"derivedFrom":[subQ0,sQuery(id+"F0.wireOp",EDGE,"E15")]}),-1.0]])],"derivedFrom":subQ0})])],"isStart":false});}
            var Q5;
            {var subQ0=sQuery(id+"F0.wireOp",EDGE,"E1");Q5=makeQuery(id+"F2.opExtrude","CAP_EDGE",EDGE,{"disambiguationData":[OSD([subQ0]),TDD([makeQuery(id+"F0.imprint","IMPRINT",EDGE,{"disambiguationData":[TD([[makeQuery(id+"F0.imprint","INTERSECT",VERTEX,{"derivedFrom":[subQ0,sQuery(id+"F0.wireOp",EDGE,"E7")]}),-1.0]])],"derivedFrom":subQ0})])],"isStart":false});}
            chamfer(context, id + "F4", {"entities" : qUnion([Q0, Q1, Q2, Q3, Q4, Q5]), "chamferType" : ChamferType.TWO_OFFSETS, "width1" : 4 * mm, "oppositeDirection" : false, "width2" : 2 * mm, "tangentPropagation" : true});
        }
        {
            var Q0;
            Q0=makeQuery(id+"F3.opExtrude","SWEPT_FACE",FACE,{"disambiguationData":[OSD([sQuery(id+"F0.wireOp",EDGE,"E0")])]});
            var Q1;
            Q1=makeQuery(id+"F2.opExtrude","CAP_EDGE",EDGE,{"disambiguationData":[OSD([sQuery(id+"F0.wireOp",EDGE,"E18")])],"isStart":false});
            var Q2;
            {var subQ0=sQuery(id+"F0.wireOp",EDGE,"E1");var subQ1=makeQuery(id+"F0.imprint","IMPRINT",EDGE,{"disambiguationData":[TD([[makeQuery(id+"F0.imprint","INTERSECT",VERTEX,{"derivedFrom":[subQ0,sQuery(id+"F0.wireOp",EDGE,"E7")]}),-1.0]])],"derivedFrom":subQ0});Q2=makeQuery(id+"F4.opChamfer","BLEND_EDGE",EDGE,{"blendedFrom":[makeQuery(id+"F2.opExtrude","CAP_EDGE",EDGE,{"disambiguationData":[OSD([subQ0]),TDD([subQ1])],"isStart":false}),makeQuery(id+"F2.opExtrude","SWEPT_FACE",FACE,{"disambiguationData":[OSD([subQ0]),TDD([subQ1])]})],"blendedInto":[makeQuery(id+"F2.opExtrude","SWEPT_FACE",FACE,{"disambiguationData":[OSD([subQ0]),TDD([subQ1])]})]});}
            var Q3;
            Q3=makeQuery(id+"F2.opExtrude","SWEPT_EDGE",EDGE,{"disambiguationData":[OSD([sQuery(id+"F0.wireOp",EDGE,"E1"),sQuery(id+"F0.wireOp",EDGE,"E6")])]});
            var Q4;
            Q4=makeQuery(id+"F2.opExtrude","SWEPT_EDGE",EDGE,{"disambiguationData":[OSD([sQuery(id+"F0.wireOp",EDGE,"E1"),sQuery(id+"F0.wireOp",EDGE,"E5")])]});
            var Q5;
            {var subQ0=sQuery(id+"F0.wireOp",EDGE,"E1");var subQ1=makeQuery(id+"F0.imprint","IMPRINT",EDGE,{"disambiguationData":[TD([[makeQuery(id+"F0.imprint","INTERSECT",VERTEX,{"derivedFrom":[subQ0,sQuery(id+"F0.wireOp",EDGE,"E5")]}),-1.0]])],"derivedFrom":subQ0});Q5=makeQuery(id+"F4.opChamfer","BLEND_EDGE",EDGE,{"blendedFrom":[makeQuery(id+"F2.opExtrude","CAP_EDGE",EDGE,{"disambiguationData":[OSD([subQ0]),TDD([subQ1])],"isStart":false}),makeQuery(id+"F2.opExtrude","SWEPT_FACE",FACE,{"disambiguationData":[OSD([subQ0]),TDD([subQ1])]})],"blendedInto":[makeQuery(id+"F2.opExtrude","SWEPT_FACE",FACE,{"disambiguationData":[OSD([subQ0]),TDD([subQ1])]})]});}
            var Q6;
            {var subQ0=sQuery(id+"F0.wireOp",EDGE,"E5");var subQ1=sQuery(id+"F0.wireOp",EDGE,"E1");Q6=makeQuery(id+"F4.opChamfer","BLEND_EDGE",EDGE,{"blendedFrom":[makeQuery(id+"F2.opExtrude","CAP_EDGE",EDGE,{"disambiguationData":[OSD([subQ1]),TDD([makeQuery(id+"F0.imprint","IMPRINT",EDGE,{"disambiguationData":[TD([[makeQuery(id+"F0.imprint","INTERSECT",VERTEX,{"derivedFrom":[subQ1,subQ0]}),-1.0]])],"derivedFrom":subQ1})])],"isStart":false}),makeQuery(id+"F2.opExtrude","SWEPT_FACE",FACE,{"disambiguationData":[OSD([subQ0])]})],"blendedInto":[makeQuery(id+"F2.opExtrude","SWEPT_FACE",FACE,{"disambiguationData":[OSD([subQ0])]})]});}
            var Q7;
            {var subQ0=sQuery(id+"F0.wireOp",EDGE,"E6");var subQ1=sQuery(id+"F0.wireOp",EDGE,"E1");Q7=makeQuery(id+"F4.opChamfer","BLEND_EDGE",EDGE,{"blendedFrom":[makeQuery(id+"F2.opExtrude","CAP_EDGE",EDGE,{"disambiguationData":[OSD([subQ1]),TDD([makeQuery(id+"F0.imprint","IMPRINT",EDGE,{"disambiguationData":[TD([[makeQuery(id+"F0.imprint","INTERSECT",VERTEX,{"derivedFrom":[subQ1,sQuery(id+"F0.wireOp",EDGE,"E5")]}),-1.0]])],"derivedFrom":subQ1})])],"isStart":false}),makeQuery(id+"F2.opExtrude","SWEPT_FACE",FACE,{"disambiguationData":[OSD([subQ0])]})],"blendedInto":[makeQuery(id+"F2.opExtrude","SWEPT_FACE",FACE,{"disambiguationData":[OSD([subQ0])]})]});}
            var Q8;
            {var subQ0=sQuery(id+"F0.wireOp",EDGE,"E7");var subQ1=sQuery(id+"F0.wireOp",EDGE,"E1");Q8=makeQuery(id+"F4.opChamfer","BLEND_EDGE",EDGE,{"blendedFrom":[makeQuery(id+"F2.opExtrude","CAP_EDGE",EDGE,{"disambiguationData":[OSD([subQ1]),TDD([makeQuery(id+"F0.imprint","IMPRINT",EDGE,{"disambiguationData":[TD([[makeQuery(id+"F0.imprint","INTERSECT",VERTEX,{"derivedFrom":[subQ1,subQ0]}),-1.0]])],"derivedFrom":subQ1})])],"isStart":false}),makeQuery(id+"F2.opExtrude","SWEPT_FACE",FACE,{"disambiguationData":[OSD([subQ0])]})],"blendedInto":[makeQuery(id+"F2.opExtrude","SWEPT_FACE",FACE,{"disambiguationData":[OSD([subQ0])]})]});}
            var Q9;
            {var subQ0=sQuery(id+"F0.wireOp",EDGE,"E8");var subQ1=sQuery(id+"F0.wireOp",EDGE,"E1");Q9=makeQuery(id+"F4.opChamfer","BLEND_EDGE",EDGE,{"blendedFrom":[makeQuery(id+"F2.opExtrude","CAP_EDGE",EDGE,{"disambiguationData":[OSD([subQ1]),TDD([makeQuery(id+"F0.imprint","IMPRINT",EDGE,{"disambiguationData":[TD([[makeQuery(id+"F0.imprint","INTERSECT",VERTEX,{"derivedFrom":[subQ1,sQuery(id+"F0.wireOp",EDGE,"E7")]}),-1.0]])],"derivedFrom":subQ1})])],"isStart":false}),makeQuery(id+"F2.opExtrude","SWEPT_FACE",FACE,{"disambiguationData":[OSD([subQ0])]})],"blendedInto":[makeQuery(id+"F2.opExtrude","SWEPT_FACE",FACE,{"disambiguationData":[OSD([subQ0])]})]});}
            var Q10;
            {var subQ0=sQuery(id+"F0.wireOp",EDGE,"E15");var subQ1=sQuery(id+"F0.wireOp",EDGE,"E1");Q10=makeQuery(id+"F4.opChamfer","BLEND_EDGE",EDGE,{"blendedFrom":[makeQuery(id+"F2.opExtrude","CAP_EDGE",EDGE,{"disambiguationData":[OSD([subQ1]),TDD([makeQuery(id+"F0.imprint","IMPRINT",EDGE,{"disambiguationData":[TD([[makeQuery(id+"F0.imprint","INTERSECT",VERTEX,{"derivedFrom":[subQ1,subQ0]}),-1.0]])],"derivedFrom":subQ1})])],"isStart":false}),makeQuery(id+"F2.opExtrude","SWEPT_FACE",FACE,{"disambiguationData":[OSD([subQ0])]})],"blendedInto":[makeQuery(id+"F2.opExtrude","SWEPT_FACE",FACE,{"disambiguationData":[OSD([subQ0])]})]});}
            var Q11;
            {var subQ0=sQuery(id+"F0.wireOp",EDGE,"E1");var subQ1=makeQuery(id+"F0.imprint","IMPRINT",EDGE,{"disambiguationData":[TD([[makeQuery(id+"F0.imprint","INTERSECT",VERTEX,{"derivedFrom":[subQ0,sQuery(id+"F0.wireOp",EDGE,"E15")]}),-1.0]])],"derivedFrom":subQ0});Q11=makeQuery(id+"F4.opChamfer","BLEND_EDGE",EDGE,{"blendedFrom":[makeQuery(id+"F2.opExtrude","CAP_EDGE",EDGE,{"disambiguationData":[OSD([subQ0]),TDD([subQ1])],"isStart":false}),makeQuery(id+"F2.opExtrude","SWEPT_FACE",FACE,{"disambiguationData":[OSD([subQ0]),TDD([subQ1])]})],"blendedInto":[makeQuery(id+"F2.opExtrude","SWEPT_FACE",FACE,{"disambiguationData":[OSD([subQ0]),TDD([subQ1])]})]});}
            var Q12;
            {var subQ0=sQuery(id+"F0.wireOp",EDGE,"E16");var subQ1=sQuery(id+"F0.wireOp",EDGE,"E1");Q12=makeQuery(id+"F4.opChamfer","BLEND_EDGE",EDGE,{"blendedFrom":[makeQuery(id+"F2.opExtrude","CAP_EDGE",EDGE,{"disambiguationData":[OSD([subQ1]),TDD([makeQuery(id+"F0.imprint","IMPRINT",EDGE,{"disambiguationData":[TD([[makeQuery(id+"F0.imprint","INTERSECT",VERTEX,{"derivedFrom":[subQ1,sQuery(id+"F0.wireOp",EDGE,"E15")]}),-1.0]])],"derivedFrom":subQ1})])],"isStart":false}),makeQuery(id+"F2.opExtrude","SWEPT_FACE",FACE,{"disambiguationData":[OSD([subQ0])]})],"blendedInto":[makeQuery(id+"F2.opExtrude","SWEPT_FACE",FACE,{"disambiguationData":[OSD([subQ0])]})]});}
            var Q13;
            Q13=makeQuery(id+"F2.opExtrude","SWEPT_EDGE",EDGE,{"disambiguationData":[OSD([sQuery(id+"F0.wireOp",EDGE,"E1"),sQuery(id+"F0.wireOp",EDGE,"E16")])]});
            var Q14;
            Q14=makeQuery(id+"F2.opExtrude","SWEPT_EDGE",EDGE,{"disambiguationData":[OSD([sQuery(id+"F0.wireOp",EDGE,"E1"),sQuery(id+"F0.wireOp",EDGE,"E15")])]});
            var Q15;
            {var subQ0=sQuery(id+"F0.wireOp",EDGE,"E1");Q15=makeQuery(id+"F2.opExtrude","SWEPT_FACE",FACE,{"disambiguationData":[OSD([subQ0]),TDD([makeQuery(id+"F0.imprint","IMPRINT",EDGE,{"disambiguationData":[TD([[makeQuery(id+"F0.imprint","INTERSECT",VERTEX,{"derivedFrom":[subQ0,sQuery(id+"F0.wireOp",EDGE,"E13")]}),-1.0]])],"derivedFrom":subQ0})])]});}
            var Q16;
            {var subQ0=sQuery(id+"F0.wireOp",EDGE,"E13");var subQ1=sQuery(id+"F0.wireOp",EDGE,"E1");Q16=makeQuery(id+"F4.opChamfer","BLEND_EDGE",EDGE,{"blendedFrom":[makeQuery(id+"F2.opExtrude","CAP_EDGE",EDGE,{"disambiguationData":[OSD([subQ1]),TDD([makeQuery(id+"F0.imprint","IMPRINT",EDGE,{"disambiguationData":[TD([[makeQuery(id+"F0.imprint","INTERSECT",VERTEX,{"derivedFrom":[subQ1,subQ0]}),-1.0]])],"derivedFrom":subQ1})])],"isStart":false}),makeQuery(id+"F2.opExtrude","SWEPT_FACE",FACE,{"disambiguationData":[OSD([subQ0])]})],"blendedInto":[makeQuery(id+"F2.opExtrude","SWEPT_FACE",FACE,{"disambiguationData":[OSD([subQ0])]})]});}
            var Q17;
            {var subQ0=sQuery(id+"F0.wireOp",EDGE,"E14");var subQ1=sQuery(id+"F0.wireOp",EDGE,"E1");Q17=makeQuery(id+"F4.opChamfer","BLEND_EDGE",EDGE,{"blendedFrom":[makeQuery(id+"F2.opExtrude","CAP_EDGE",EDGE,{"disambiguationData":[OSD([subQ1]),TDD([makeQuery(id+"F0.imprint","IMPRINT",EDGE,{"disambiguationData":[TD([[makeQuery(id+"F0.imprint","INTERSECT",VERTEX,{"derivedFrom":[subQ1,sQuery(id+"F0.wireOp",EDGE,"E13")]}),-1.0]])],"derivedFrom":subQ1})])],"isStart":false}),makeQuery(id+"F2.opExtrude","SWEPT_FACE",FACE,{"disambiguationData":[OSD([subQ0])]})],"blendedInto":[makeQuery(id+"F2.opExtrude","SWEPT_FACE",FACE,{"disambiguationData":[OSD([subQ0])]})]});}
            var Q18;
            {var subQ0=sQuery(id+"F0.wireOp",EDGE,"E1");Q18=makeQuery(id+"F2.opExtrude","SWEPT_FACE",FACE,{"disambiguationData":[OSD([subQ0]),TDD([makeQuery(id+"F0.imprint","IMPRINT",EDGE,{"disambiguationData":[TD([[makeQuery(id+"F0.imprint","INTERSECT",VERTEX,{"derivedFrom":[subQ0,sQuery(id+"F0.wireOp",EDGE,"E11")]}),-1.0]])],"derivedFrom":subQ0})])]});}
            var Q19;
            {var subQ0=sQuery(id+"F0.wireOp",EDGE,"E12");var subQ1=sQuery(id+"F0.wireOp",EDGE,"E1");Q19=makeQuery(id+"F4.opChamfer","BLEND_EDGE",EDGE,{"blendedFrom":[makeQuery(id+"F2.opExtrude","CAP_EDGE",EDGE,{"disambiguationData":[OSD([subQ1]),TDD([makeQuery(id+"F0.imprint","IMPRINT",EDGE,{"disambiguationData":[TD([[makeQuery(id+"F0.imprint","INTERSECT",VERTEX,{"derivedFrom":[subQ1,sQuery(id+"F0.wireOp",EDGE,"E11")]}),-1.0]])],"derivedFrom":subQ1})])],"isStart":false}),makeQuery(id+"F2.opExtrude","SWEPT_FACE",FACE,{"disambiguationData":[OSD([subQ0])]})],"blendedInto":[makeQuery(id+"F2.opExtrude","SWEPT_FACE",FACE,{"disambiguationData":[OSD([subQ0])]})]});}
            var Q20;
            {var subQ0=sQuery(id+"F0.wireOp",EDGE,"E11");var subQ1=sQuery(id+"F0.wireOp",EDGE,"E1");Q20=makeQuery(id+"F4.opChamfer","BLEND_EDGE",EDGE,{"blendedFrom":[makeQuery(id+"F2.opExtrude","CAP_EDGE",EDGE,{"disambiguationData":[OSD([subQ1]),TDD([makeQuery(id+"F0.imprint","IMPRINT",EDGE,{"disambiguationData":[TD([[makeQuery(id+"F0.imprint","INTERSECT",VERTEX,{"derivedFrom":[subQ1,subQ0]}),-1.0]])],"derivedFrom":subQ1})])],"isStart":false}),makeQuery(id+"F2.opExtrude","SWEPT_FACE",FACE,{"disambiguationData":[OSD([subQ0])]})],"blendedInto":[makeQuery(id+"F2.opExtrude","SWEPT_FACE",FACE,{"disambiguationData":[OSD([subQ0])]})]});}
            var Q21;
            {var subQ0=sQuery(id+"F0.wireOp",EDGE,"E1");Q21=makeQuery(id+"F2.opExtrude","SWEPT_FACE",FACE,{"disambiguationData":[OSD([subQ0]),TDD([makeQuery(id+"F0.imprint","IMPRINT",EDGE,{"disambiguationData":[TD([[makeQuery(id+"F0.imprint","INTERSECT",VERTEX,{"derivedFrom":[subQ0,sQuery(id+"F0.wireOp",EDGE,"E10")]}),1.0]])],"derivedFrom":subQ0})])]});}
            var Q22;
            {var subQ0=sQuery(id+"F0.wireOp",EDGE,"E10");var subQ1=sQuery(id+"F0.wireOp",EDGE,"E1");Q22=makeQuery(id+"F4.opChamfer","BLEND_EDGE",EDGE,{"blendedFrom":[makeQuery(id+"F2.opExtrude","CAP_EDGE",EDGE,{"disambiguationData":[OSD([subQ1]),TDD([makeQuery(id+"F0.imprint","IMPRINT",EDGE,{"disambiguationData":[TD([[makeQuery(id+"F0.imprint","INTERSECT",VERTEX,{"derivedFrom":[subQ1,subQ0]}),1.0]])],"derivedFrom":subQ1})])],"isStart":false}),makeQuery(id+"F2.opExtrude","SWEPT_FACE",FACE,{"disambiguationData":[OSD([subQ0])]})],"blendedInto":[makeQuery(id+"F2.opExtrude","SWEPT_FACE",FACE,{"disambiguationData":[OSD([subQ0])]})]});}
            var Q23;
            {var subQ0=sQuery(id+"F0.wireOp",EDGE,"E9");var subQ1=sQuery(id+"F0.wireOp",EDGE,"E1");Q23=makeQuery(id+"F4.opChamfer","BLEND_EDGE",EDGE,{"blendedFrom":[makeQuery(id+"F2.opExtrude","CAP_EDGE",EDGE,{"disambiguationData":[OSD([subQ1]),TDD([makeQuery(id+"F0.imprint","IMPRINT",EDGE,{"disambiguationData":[TD([[makeQuery(id+"F0.imprint","INTERSECT",VERTEX,{"derivedFrom":[subQ1,sQuery(id+"F0.wireOp",EDGE,"E10")]}),1.0]])],"derivedFrom":subQ1})])],"isStart":false}),makeQuery(id+"F2.opExtrude","SWEPT_FACE",FACE,{"disambiguationData":[OSD([subQ0])]})],"blendedInto":[makeQuery(id+"F2.opExtrude","SWEPT_FACE",FACE,{"disambiguationData":[OSD([subQ0])]})]});}
            var Q24;
            {var subQ0=sQuery(id+"F0.wireOp",EDGE,"E17");Q24=makeQuery(id+"F2.opExtrude","SWEPT_FACE",FACE,{"disambiguationData":[OSD([subQ0]),TDD([makeQuery(id+"F0.imprint","IMPRINT",EDGE,{"disambiguationData":[TD([[makeQuery(id+"F0.imprint","INTERSECT",VERTEX,{"derivedFrom":[sQuery(id+"F0.wireOp",EDGE,"E5"),subQ0]}),1.0]])],"derivedFrom":subQ0})])]});}
            var Q25;
            {var subQ0=sQuery(id+"F0.wireOp",EDGE,"E17");Q25=makeQuery(id+"F2.opExtrude","SWEPT_FACE",FACE,{"disambiguationData":[OSD([subQ0]),TDD([makeQuery(id+"F0.imprint","IMPRINT",EDGE,{"disambiguationData":[TD([[makeQuery(id+"F0.imprint","INTERSECT",VERTEX,{"derivedFrom":[sQuery(id+"F0.wireOp",EDGE,"E6"),subQ0]}),-1.0]])],"derivedFrom":subQ0})])]});}
            var Q26;
            {var subQ0=sQuery(id+"F0.wireOp",EDGE,"E17");Q26=makeQuery(id+"F2.opExtrude","SWEPT_FACE",FACE,{"disambiguationData":[OSD([subQ0]),TDD([makeQuery(id+"F0.imprint","IMPRINT",EDGE,{"disambiguationData":[TD([[makeQuery(id+"F0.imprint","INTERSECT",VERTEX,{"derivedFrom":[sQuery(id+"F0.wireOp",EDGE,"E8"),subQ0]}),-1.0]])],"derivedFrom":subQ0})])]});}
            var Q27;
            {var subQ0=sQuery(id+"F0.wireOp",EDGE,"E17");Q27=makeQuery(id+"F2.opExtrude","SWEPT_FACE",FACE,{"disambiguationData":[OSD([subQ0]),TDD([makeQuery(id+"F0.imprint","IMPRINT",EDGE,{"disambiguationData":[TD([[makeQuery(id+"F0.imprint","INTERSECT",VERTEX,{"derivedFrom":[sQuery(id+"F0.wireOp",EDGE,"E10"),subQ0]}),-1.0]])],"derivedFrom":subQ0})])]});}
            var Q28;
            {var subQ0=sQuery(id+"F0.wireOp",EDGE,"E17");Q28=makeQuery(id+"F2.opExtrude","SWEPT_FACE",FACE,{"disambiguationData":[OSD([subQ0]),TDD([makeQuery(id+"F0.imprint","IMPRINT",EDGE,{"disambiguationData":[TD([[makeQuery(id+"F0.imprint","INTERSECT",VERTEX,{"derivedFrom":[sQuery(id+"F0.wireOp",EDGE,"E12"),subQ0]}),-1.0]])],"derivedFrom":subQ0})])]});}
            var Q29;
            {var subQ0=sQuery(id+"F0.wireOp",EDGE,"E17");Q29=makeQuery(id+"F2.opExtrude","SWEPT_FACE",FACE,{"disambiguationData":[OSD([subQ0]),TDD([makeQuery(id+"F0.imprint","IMPRINT",EDGE,{"disambiguationData":[TD([[makeQuery(id+"F0.imprint","INTERSECT",VERTEX,{"derivedFrom":[sQuery(id+"F0.wireOp",EDGE,"E14"),subQ0]}),-1.0]])],"derivedFrom":subQ0})])]});}
            var Q30;
            Q30=makeQuery(id+"F3.opExtrude","CAP_EDGE",EDGE,{"disambiguationData":[OSD([sQuery(id+"F0.wireOp",EDGE,"E3.left")])],"isStart":true});
            var Q31;
            Q31=makeQuery(id+"F3.opExtrude","CAP_EDGE",EDGE,{"disambiguationData":[OSD([sQuery(id+"F0.wireOp",EDGE,"E3.right")])],"isStart":true});
            var Q32;
            Q32=makeQuery(id+"F3.opExtrude","CAP_EDGE",EDGE,{"disambiguationData":[OSD([sQuery(id+"F0.wireOp",EDGE,"E3.top")])],"isStart":true});
            var Q33;
            Q33=makeQuery(id+"F3.opExtrude","CAP_EDGE",EDGE,{"disambiguationData":[OSD([sQuery(id+"F0.wireOp",EDGE,"E3.bottom")])],"isStart":true});
            fillet(context, id + "F5", {"entities" : qUnion([Q0, Q1, Q2, Q3, Q4, Q5, Q6, Q7, Q8, Q9, Q10, Q11, Q12, Q13, Q14, Q15, Q16, Q17, Q18, Q19, Q20, Q21, Q22, Q23, Q24, Q25, Q26, Q27, Q28, Q29, Q30, Q31, Q32, Q33]), "radius" : 0.3 * mm, "tangentPropagation" : true, "defaultsChanged" : true, "vertexSettings" : [], "allowEdgeOverflow" : false});
        }
    });
